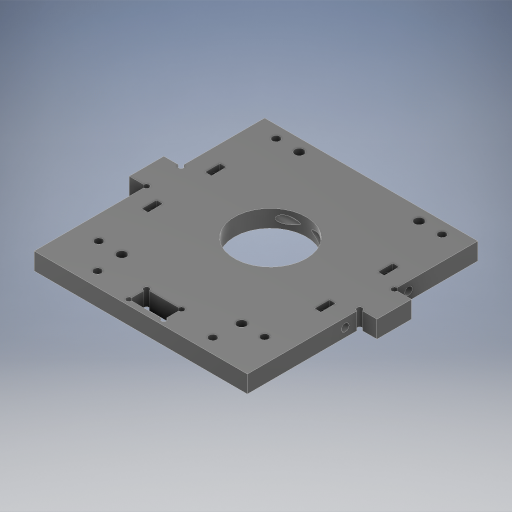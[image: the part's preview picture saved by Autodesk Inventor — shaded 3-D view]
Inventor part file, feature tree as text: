
AUTODESK INVENTOR PART (.ipt)
format: ipt  version: 2024 (Build 280153000, 153)  size: 411,136 bytes
history: native  units: in
note: dims shown in document units (in); Inventor stores cm internally (conversion verified against a paired STEP export)
features: extrude x6, sketch x6, other x4, projected_geometry x1
ambient origin geometry x4: Origin, X Axis, Y Axis, Z Axis
bodies: Body1 (feature_tree)
feature tree (17):
  other  "솔리드1"
  extrude  "돌출1"  Depth=2.9134in
  extrude  "돌출2"  Depth=2.7559in
  extrude  "돌출3"  Depth=0.0866in
  extrude  "돌출4"  Depth=0.2047in
  extrude  "돌출5"  Depth=0.0866in
  extrude  "돌출6"  Depth=0.2047in
  other  "우측면도"
  other  "평면도"
  other  "정면도"
  sketch  "스케치1"
  sketch  "스케치2"
  sketch  "스케치3"
  sketch  "스케치4"
  sketch  "스케치5"
  sketch  "스케치6"
  projected_geometry  "투영된 루프1"
